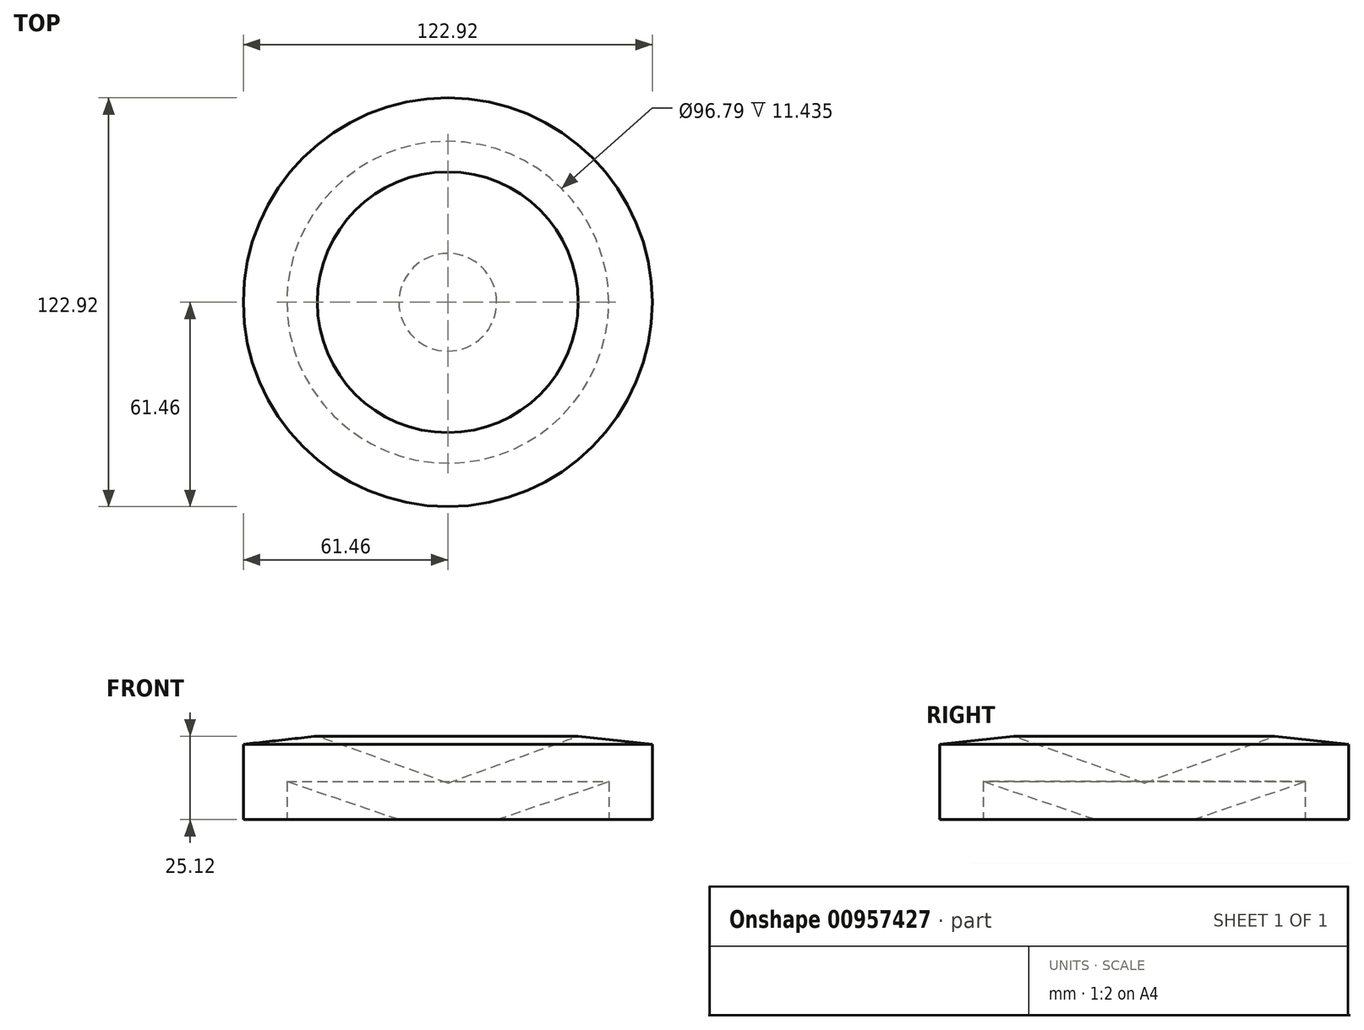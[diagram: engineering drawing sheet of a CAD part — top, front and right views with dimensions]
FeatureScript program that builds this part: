
annotation { "Feature Type Name" : "Feature", "Feature Type Description" : "" }
export const myFeature = defineFeature(function(context is Context, id is Id, definition is map)
    precondition{}
    {
        {
            var Q0;
            Q0=qCreatedBy(makeId("Front.planeOp"),FACE);
            var sketch = newSketch(context, id + "F0", { "sketchPlane" : qUnion([Q0])});
            skLineSegment(sketch, "E0", {"start": v(-61.46, 22.67) * mm, "end": v(-61.46, 0) * mm});
            skLineSegment(sketch, "E1", {"start": v(-61.46, 0) * mm, "end": v(-48.4, 0) * mm});
            skLineSegment(sketch, "E2", {"start": v(-48.4, 0) * mm, "end": v(-48.4, 11.43) * mm});
            skLineSegment(sketch, "E3", {"start": v(-48.4, 11.43) * mm, "end": v(-14.7, 0) * mm});
            skLineSegment(sketch, "E4", {"start": v(-14.7, 0) * mm, "end": v(0, 0) * mm});
            skLineSegment(sketch, "E5", {"start": v(0, 0) * mm, "end": v(0, 11.03) * mm});
            skLineSegment(sketch, "E6", {"start": v(0, 11.03) * mm, "end": v(-39.2, 25.12) * mm});
            skLineSegment(sketch, "E7", {"start": v(-39.2, 25.12) * mm, "end": v(-61.46, 22.67) * mm});
            skSolve(sketch);
        }
        {
            var Q0;
            Q0=makeQuery(id+"F0.imprint","IMPRINT",FACE,{"disambiguationData":[TD([[makeQuery(id+"F0.imprint","IMPRINT",EDGE,{"derivedFrom":sQuery(id+"F0.wireOp",EDGE,"E0")}),1.0]])]});
            var Q1;
            Q1=sQuery(id+"F0.wireOp",EDGE,"E5");
            revolve(context, id + "F1", {"surfaceOperationType" : NewSurfaceOperationType.NEW, "entities" : qUnion([Q0]), "axis" : qUnion([Q1]), "revolveType" : RevolveType.FULL});
        }
    });
